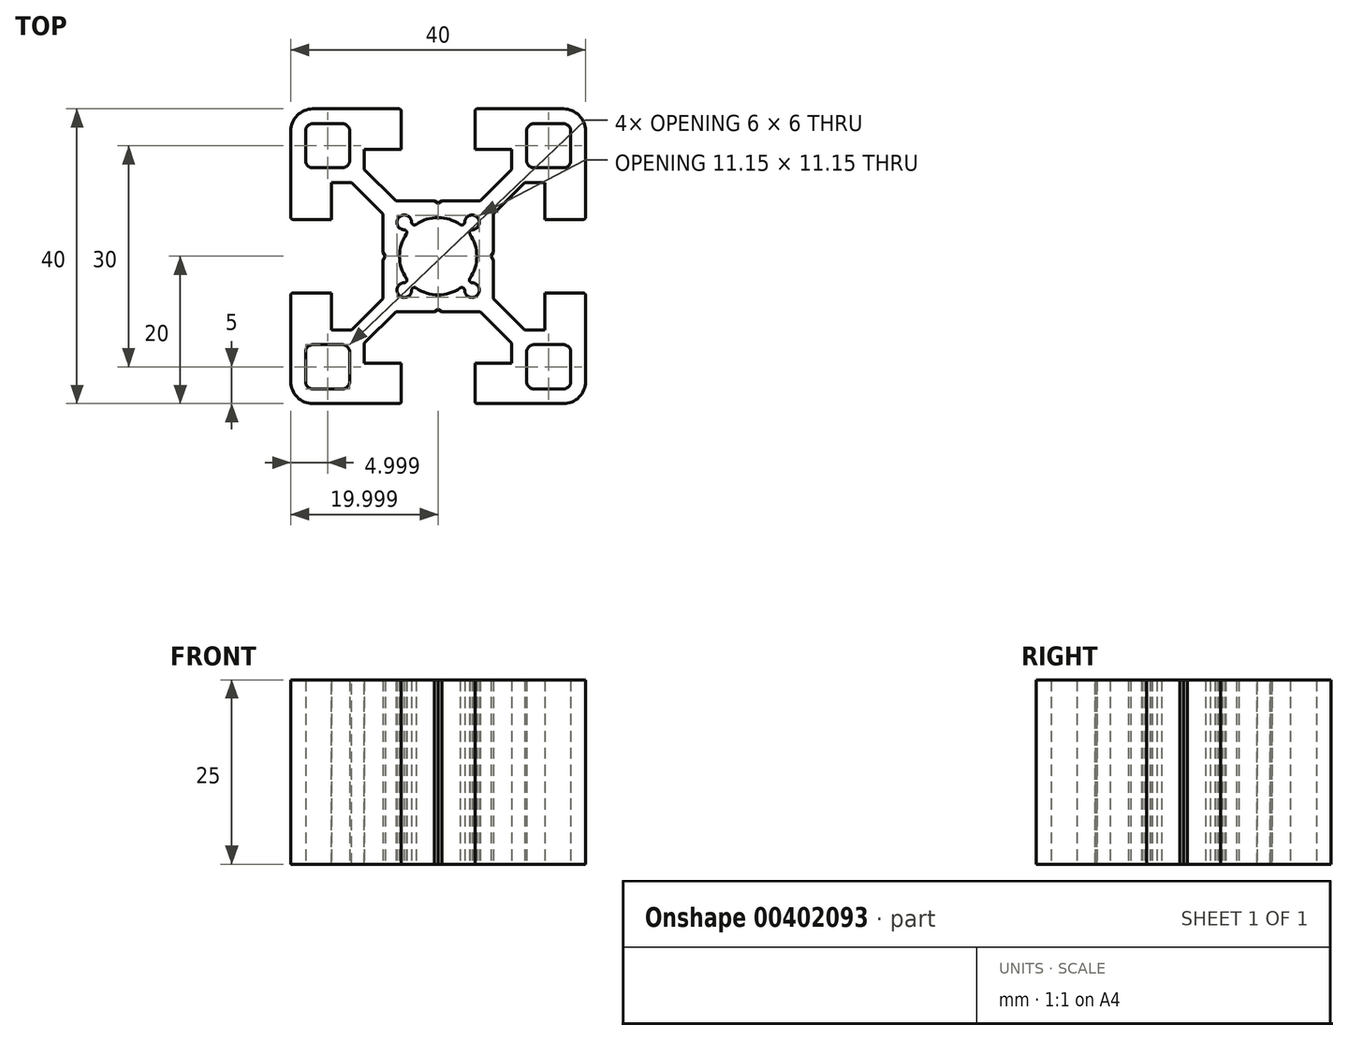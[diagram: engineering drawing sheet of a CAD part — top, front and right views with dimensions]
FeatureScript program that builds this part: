
annotation { "Feature Type Name" : "Feature", "Feature Type Description" : "" }
export const myFeature = defineFeature(function(context is Context, id is Id, definition is map)
    precondition{}
    {
        {
            var Q0;
            Q0=qCreatedBy(makeId("Top.planeOp"),FACE);
            var sketch = newSketch(context, id + "F0", { "sketchPlane" : qUnion([Q0]) });
            skLineSegment(sketch, "E0", {"start": v(-45.88, 30.5) * mm, "end": v(-49.88, 30.5) * mm});
            skArc(sketch, "E1", {"start": v(-13.18, 17.5) * mm, "mid": v(-12.97, 17.59) * mm, "end": v(-12.88, 17.8) * mm});
            skLineSegment(sketch, "E2", {"start": v(-13.18, 17.5) * mm, "end": v(-18.38, 17.5) * mm});
            skLineSegment(sketch, "E3", {"start": v(-18.38, 22.5) * mm, "end": v(-18.38, 17.5) * mm});
            skLineSegment(sketch, "E4", {"start": v(-12.88, 29.5) * mm, "end": v(-12.88, 17.8) * mm});
            skLineSegment(sketch, "E5", {"start": v(-14.88, 29.5) * mm, "end": v(-14.88, 25.5) * mm});
            skArc(sketch, "E6", {"start": v(-14.88, 29.5) * mm, "mid": v(-15.17, 30.2) * mm, "end": v(-15.88, 30.5) * mm});
            skArc(sketch, "E7", {"start": v(-12.88, 7.2) * mm, "mid": v(-12.97, 7.41) * mm, "end": v(-13.18, 7.5) * mm});
            skLineSegment(sketch, "E8", {"start": v(-18.38, 2.5) * mm, "end": v(-18.38, 7.5) * mm});
            skLineSegment(sketch, "E9", {"start": v(-13.18, 7.5) * mm, "end": v(-18.38, 7.5) * mm});
            skLineSegment(sketch, "E10", {"start": v(-12.88, -4.5) * mm, "end": v(-12.88, 7.2) * mm});
            skLineSegment(sketch, "E11", {"start": v(-14.88, -4.5) * mm, "end": v(-14.88, -0.5) * mm});
            skArc(sketch, "E12", {"start": v(-14.88, -0.5) * mm, "mid": v(-15.17, 0.2) * mm, "end": v(-15.88, 0.5) * mm});
            skLineSegment(sketch, "E13", {"start": v(-49.88, 32.5) * mm, "end": v(-38.18, 32.5) * mm});
            skArc(sketch, "E14", {"start": v(-20.88, 25.5) * mm, "mid": v(-20.59, 24.8) * mm, "end": v(-19.88, 24.5) * mm});
            skLineSegment(sketch, "E15", {"start": v(-22.88, 27) * mm, "end": v(-22.88, 24.27) * mm});
            skLineSegment(sketch, "E16", {"start": v(-22.88, 27) * mm, "end": v(-27.88, 27) * mm});
            skLineSegment(sketch, "E17", {"start": v(-22.88, 24.27) * mm, "end": v(-27.15, 20) * mm});
            skLineSegment(sketch, "E18", {"start": v(-21.11, 22.5) * mm, "end": v(-25.38, 18.23) * mm});
            skLineSegment(sketch, "E19", {"start": v(-42.88, 27) * mm, "end": v(-42.88, 24.27) * mm});
            skLineSegment(sketch, "E20", {"start": v(-42.88, 27) * mm, "end": v(-37.88, 27) * mm});
            skLineSegment(sketch, "E21", {"start": v(-42.88, 24.27) * mm, "end": v(-38.61, 20) * mm});
            skLineSegment(sketch, "E22", {"start": v(-47.38, 22.5) * mm, "end": v(-44.65, 22.5) * mm});
            skArc(sketch, "E23", {"start": v(-52.88, 17.8) * mm, "mid": v(-52.8, 17.59) * mm, "end": v(-52.58, 17.5) * mm});
            skLineSegment(sketch, "E24", {"start": v(-52.58, 17.5) * mm, "end": v(-47.38, 17.5) * mm});
            skLineSegment(sketch, "E25", {"start": v(-44.65, 22.5) * mm, "end": v(-40.38, 18.23) * mm});
            skLineSegment(sketch, "E26", {"start": v(-47.38, 17.5) * mm, "end": v(-47.38, 22.5) * mm});
            skLineSegment(sketch, "E27", {"start": v(-52.88, 29.5) * mm, "end": v(-52.88, 17.8) * mm});
            skLineSegment(sketch, "E28", {"start": v(-50.88, 29.5) * mm, "end": v(-50.88, 25.5) * mm});
            skLineSegment(sketch, "E29", {"start": v(-44.88, 29.5) * mm, "end": v(-44.88, 25.5) * mm});
            skArc(sketch, "E30", {"start": v(-45.88, 24.5) * mm, "mid": v(-45.17, 24.8) * mm, "end": v(-44.88, 25.5) * mm});
            skArc(sketch, "E31", {"start": v(-44.88, 29.5) * mm, "mid": v(-45.17, 30.2) * mm, "end": v(-45.88, 30.5) * mm});
            skLineSegment(sketch, "E32", {"start": v(-37.88, 32.2) * mm, "end": v(-37.88, 27) * mm});
            skLineSegment(sketch, "E33", {"start": v(-27.88, 32.2) * mm, "end": v(-27.88, 27) * mm});
            skLineSegment(sketch, "E34", {"start": v(-20.88, 29.5) * mm, "end": v(-20.88, 25.5) * mm});
            skLineSegment(sketch, "E35", {"start": v(-21.11, 2.5) * mm, "end": v(-25.38, 6.77) * mm});
            skLineSegment(sketch, "E36", {"start": v(-22.88, -2) * mm, "end": v(-22.88, 0.73) * mm});
            skLineSegment(sketch, "E37", {"start": v(-22.88, 0.73) * mm, "end": v(-27.15, 5) * mm});
            skLineSegment(sketch, "E38", {"start": v(-27.88, -7.2) * mm, "end": v(-27.88, -2) * mm});
            skLineSegment(sketch, "E39", {"start": v(-20.88, -4.5) * mm, "end": v(-20.88, -0.5) * mm});
            skArc(sketch, "E40", {"start": v(-20.88, -4.5) * mm, "mid": v(-20.59, -5.2) * mm, "end": v(-19.88, -5.5) * mm});
            skLineSegment(sketch, "E41", {"start": v(-44.65, 2.5) * mm, "end": v(-40.38, 6.77) * mm});
            skLineSegment(sketch, "E42", {"start": v(-42.88, -2) * mm, "end": v(-42.88, 0.73) * mm});
            skLineSegment(sketch, "E43", {"start": v(-42.88, -2) * mm, "end": v(-37.88, -2) * mm});
            skLineSegment(sketch, "E44", {"start": v(-38.61, 5) * mm, "end": v(-33.4, 5) * mm});
            skLineSegment(sketch, "E45", {"start": v(-42.88, 0.73) * mm, "end": v(-38.61, 5) * mm});
            skLineSegment(sketch, "E46", {"start": v(-47.38, 7.5) * mm, "end": v(-47.38, 2.5) * mm});
            skArc(sketch, "E47", {"start": v(-52.58, 7.5) * mm, "mid": v(-52.8, 7.41) * mm, "end": v(-52.88, 7.2) * mm});
            skLineSegment(sketch, "E48", {"start": v(-52.58, 7.5) * mm, "end": v(-47.38, 7.5) * mm});
            skLineSegment(sketch, "E49", {"start": v(-49.88, 0.5) * mm, "end": v(-45.88, 0.5) * mm});
            skArc(sketch, "E50", {"start": v(-44.88, -0.5) * mm, "mid": v(-45.17, 0.2) * mm, "end": v(-45.88, 0.5) * mm});
            skLineSegment(sketch, "E51", {"start": v(-47.38, 2.5) * mm, "end": v(-44.65, 2.5) * mm});
            skLineSegment(sketch, "E52", {"start": v(-49.88, -5.5) * mm, "end": v(-45.88, -5.5) * mm});
            skArc(sketch, "E53", {"start": v(-50.88, -4.5) * mm, "mid": v(-50.59, -5.2) * mm, "end": v(-49.88, -5.5) * mm});
            skLineSegment(sketch, "E54", {"start": v(-49.88, -7.5) * mm, "end": v(-38.18, -7.5) * mm});
            skArc(sketch, "E55", {"start": v(-45.88, -5.5) * mm, "mid": v(-45.17, -5.2) * mm, "end": v(-44.88, -4.5) * mm});
            skLineSegment(sketch, "E56", {"start": v(-52.88, -4.5) * mm, "end": v(-52.88, 7.2) * mm});
            skLineSegment(sketch, "E57", {"start": v(-50.88, -4.5) * mm, "end": v(-50.88, -0.5) * mm});
            skArc(sketch, "E58", {"start": v(-49.88, 0.5) * mm, "mid": v(-50.59, 0.2) * mm, "end": v(-50.88, -0.5) * mm});
            skLineSegment(sketch, "E59", {"start": v(-44.88, -4.5) * mm, "end": v(-44.88, -0.5) * mm});
            skLineSegment(sketch, "E60", {"start": v(-37.88, -7.2) * mm, "end": v(-37.88, -2) * mm});
            skLineSegment(sketch, "E61", {"start": v(-32.88, 37.5) * mm, "end": v(-32.88, -12.5) * mm, "construction": true});
            skLineSegment(sketch, "E62", {"start": v(-25.38, 18.23) * mm, "end": v(-25.38, 13.02) * mm});
            skLineSegment(sketch, "E63", {"start": v(-15.88, 0.5) * mm, "end": v(-19.88, 0.5) * mm});
            skArc(sketch, "E64", {"start": v(-19.88, 0.5) * mm, "mid": v(-20.59, 0.2) * mm, "end": v(-20.88, -0.5) * mm});
            skLineSegment(sketch, "E65", {"start": v(-57.88, 12.5) * mm, "end": v(-7.88, 12.5) * mm, "construction": true});
            skLineSegment(sketch, "E66", {"start": v(-18.38, 2.5) * mm, "end": v(-21.11, 2.5) * mm});
            skLineSegment(sketch, "E67", {"start": v(-15.88, 24.5) * mm, "end": v(-19.88, 24.5) * mm});
            skArc(sketch, "E68", {"start": v(-15.88, 24.5) * mm, "mid": v(-15.17, 24.8) * mm, "end": v(-14.88, 25.5) * mm});
            skLineSegment(sketch, "E69", {"start": v(-18.38, 22.5) * mm, "end": v(-21.11, 22.5) * mm});
            skLineSegment(sketch, "E70", {"start": v(-40.38, 6.77) * mm, "end": v(-40.38, 11.98) * mm});
            skArc(sketch, "E71", {"start": v(-52.88, -4.5) * mm, "mid": v(-52, -6.62) * mm, "end": v(-49.88, -7.5) * mm});
            skArc(sketch, "E72", {"start": v(-38.18, -7.5) * mm, "mid": v(-37.97, -7.41) * mm, "end": v(-37.88, -7.2) * mm});
            skLineSegment(sketch, "E73", {"start": v(-45.88, 24.5) * mm, "end": v(-49.88, 24.5) * mm});
            skArc(sketch, "E74", {"start": v(-50.88, 25.5) * mm, "mid": v(-50.59, 24.8) * mm, "end": v(-49.88, 24.5) * mm});
            skArc(sketch, "E75", {"start": v(-49.88, 30.5) * mm, "mid": v(-50.59, 30.2) * mm, "end": v(-50.88, 29.5) * mm});
            skArc(sketch, "E76", {"start": v(-37.88, 32.2) * mm, "mid": v(-37.97, 32.41) * mm, "end": v(-38.18, 32.5) * mm});
            skArc(sketch, "E77", {"start": v(-49.88, 32.5) * mm, "mid": v(-52, 31.62) * mm, "end": v(-52.88, 29.5) * mm});
            skLineSegment(sketch, "E78", {"start": v(-38.61, 20) * mm, "end": v(-33.4, 20) * mm});
            skLineSegment(sketch, "E79", {"start": v(-25.38, 11.98) * mm, "end": v(-25.38, 6.77) * mm});
            skLineSegment(sketch, "E80", {"start": v(-40.38, 13.02) * mm, "end": v(-40.38, 18.23) * mm});
            skLineSegment(sketch, "E81", {"start": v(-32.36, 20) * mm, "end": v(-27.15, 20) * mm});
            skLineSegment(sketch, "E82", {"start": v(-27.58, 32.5) * mm, "end": v(-15.88, 32.5) * mm});
            skLineSegment(sketch, "E83", {"start": v(-19.88, 30.5) * mm, "end": v(-15.88, 30.5) * mm});
            skArc(sketch, "E84", {"start": v(-19.88, 30.5) * mm, "mid": v(-20.59, 30.2) * mm, "end": v(-20.88, 29.5) * mm});
            skLineSegment(sketch, "E85", {"start": v(-27.58, -7.5) * mm, "end": v(-15.88, -7.5) * mm});
            skLineSegment(sketch, "E86", {"start": v(-19.88, -5.5) * mm, "end": v(-15.88, -5.5) * mm});
            skArc(sketch, "E87", {"start": v(-15.88, -5.5) * mm, "mid": v(-15.17, -5.2) * mm, "end": v(-14.88, -4.5) * mm});
            skLineSegment(sketch, "E88", {"start": v(-27.88, -2) * mm, "end": v(-22.88, -2) * mm});
            skLineSegment(sketch, "E89", {"start": v(-32.36, 5) * mm, "end": v(-27.15, 5) * mm});
            skArc(sketch, "E90", {"start": v(-27.88, -7.2) * mm, "mid": v(-27.8, -7.41) * mm, "end": v(-27.58, -7.5) * mm});
            skArc(sketch, "E91", {"start": v(-27.58, 32.5) * mm, "mid": v(-27.8, 32.41) * mm, "end": v(-27.88, 32.2) * mm});
            skArc(sketch, "E92", {"start": v(-15.88, -7.5) * mm, "mid": v(-13.76, -6.62) * mm, "end": v(-12.88, -4.5) * mm});
            skArc(sketch, "E93", {"start": v(-12.88, 29.5) * mm, "mid": v(-13.76, 31.62) * mm, "end": v(-15.88, 32.5) * mm});
            skLineSegment(sketch, "E94", {"start": v(-25.68, 12.5) * mm, "end": v(-25.38, 13.02) * mm});
            skLineSegment(sketch, "E95", {"start": v(-25.68, 12.5) * mm, "end": v(-25.38, 11.98) * mm});
            skLineSegment(sketch, "E96", {"start": v(-40.08, 12.5) * mm, "end": v(-40.38, 13.02) * mm});
            skLineSegment(sketch, "E97", {"start": v(-40.08, 12.5) * mm, "end": v(-40.38, 11.98) * mm});
            skLineSegment(sketch, "E98", {"start": v(-32.88, 19.7) * mm, "end": v(-33.4, 20) * mm});
            skLineSegment(sketch, "E99", {"start": v(-32.88, 19.7) * mm, "end": v(-32.36, 20) * mm});
            skLineSegment(sketch, "E100", {"start": v(-32.88, 5.3) * mm, "end": v(-33.4, 5) * mm});
            skLineSegment(sketch, "E101", {"start": v(-32.88, 5.3) * mm, "end": v(-32.36, 5) * mm});
            skArc(sketch, "E102", {"start": v(-37.19, 15.5) * mm, "mid": v(-38.13, 12.5) * mm, "end": v(-37.19, 9.5) * mm});
            skArc(sketch, "E103", {"start": v(-35.88, 8.2) * mm, "mid": v(-32.88, 7.25) * mm, "end": v(-29.88, 8.2) * mm});
            skArc(sketch, "E104", {"start": v(-28.57, 9.5) * mm, "mid": v(-27.63, 12.5) * mm, "end": v(-28.57, 15.5) * mm});
            skArc(sketch, "E105", {"start": v(-29.88, 16.8) * mm, "mid": v(-32.88, 17.75) * mm, "end": v(-35.88, 16.8) * mm});
            skArc(sketch, "E106", {"start": v(-36.48, 17.1) * mm, "mid": v(-38.18, 17.8) * mm, "end": v(-37.49, 16.1) * mm});
            skArc(sketch, "E107", {"start": v(-28.27, 16.1) * mm, "mid": v(-27.58, 17.8) * mm, "end": v(-29.28, 17.1) * mm});
            skArc(sketch, "E108", {"start": v(-29.28, 7.9) * mm, "mid": v(-27.58, 7.2) * mm, "end": v(-28.27, 8.9) * mm});
            skArc(sketch, "E109", {"start": v(-37.49, 8.9) * mm, "mid": v(-38.18, 7.2) * mm, "end": v(-36.48, 7.9) * mm});
            skArc(sketch, "E110", {"start": v(-37.19, 15.5) * mm, "mid": v(-37.16, 15.89) * mm, "end": v(-37.49, 16.1) * mm});
            skArc(sketch, "E111", {"start": v(-36.48, 17.1) * mm, "mid": v(-36.27, 16.78) * mm, "end": v(-35.88, 16.8) * mm});
            skArc(sketch, "E112", {"start": v(-28.27, 16.1) * mm, "mid": v(-28.6, 15.89) * mm, "end": v(-28.57, 15.5) * mm});
            skArc(sketch, "E113", {"start": v(-29.88, 16.8) * mm, "mid": v(-29.5, 16.78) * mm, "end": v(-29.28, 17.1) * mm});
            skArc(sketch, "E114", {"start": v(-37.49, 8.9) * mm, "mid": v(-37.16, 9.11) * mm, "end": v(-37.19, 9.5) * mm});
            skArc(sketch, "E115", {"start": v(-35.88, 8.2) * mm, "mid": v(-36.27, 8.22) * mm, "end": v(-36.48, 7.9) * mm});
            skArc(sketch, "E116", {"start": v(-28.57, 9.5) * mm, "mid": v(-28.6, 9.11) * mm, "end": v(-28.27, 8.9) * mm});
            skArc(sketch, "E117", {"start": v(-29.28, 7.9) * mm, "mid": v(-29.5, 8.22) * mm, "end": v(-29.88, 8.2) * mm});
            skSolve(sketch);
        }
        {
            var Q0;
            Q0=makeQuery(id+"F0.imprint","IMPRINT",FACE,{"disambiguationData":[TD([[makeQuery(id+"F0.imprint","IMPRINT",EDGE,{"derivedFrom":sQuery(id+"F0.wireOp",EDGE,"E0")}),-1.0]])]});
            extrude(context, id + "F1", {"entities" : qUnion([Q0]), "depth" : 25 * mm});
        }
    });
